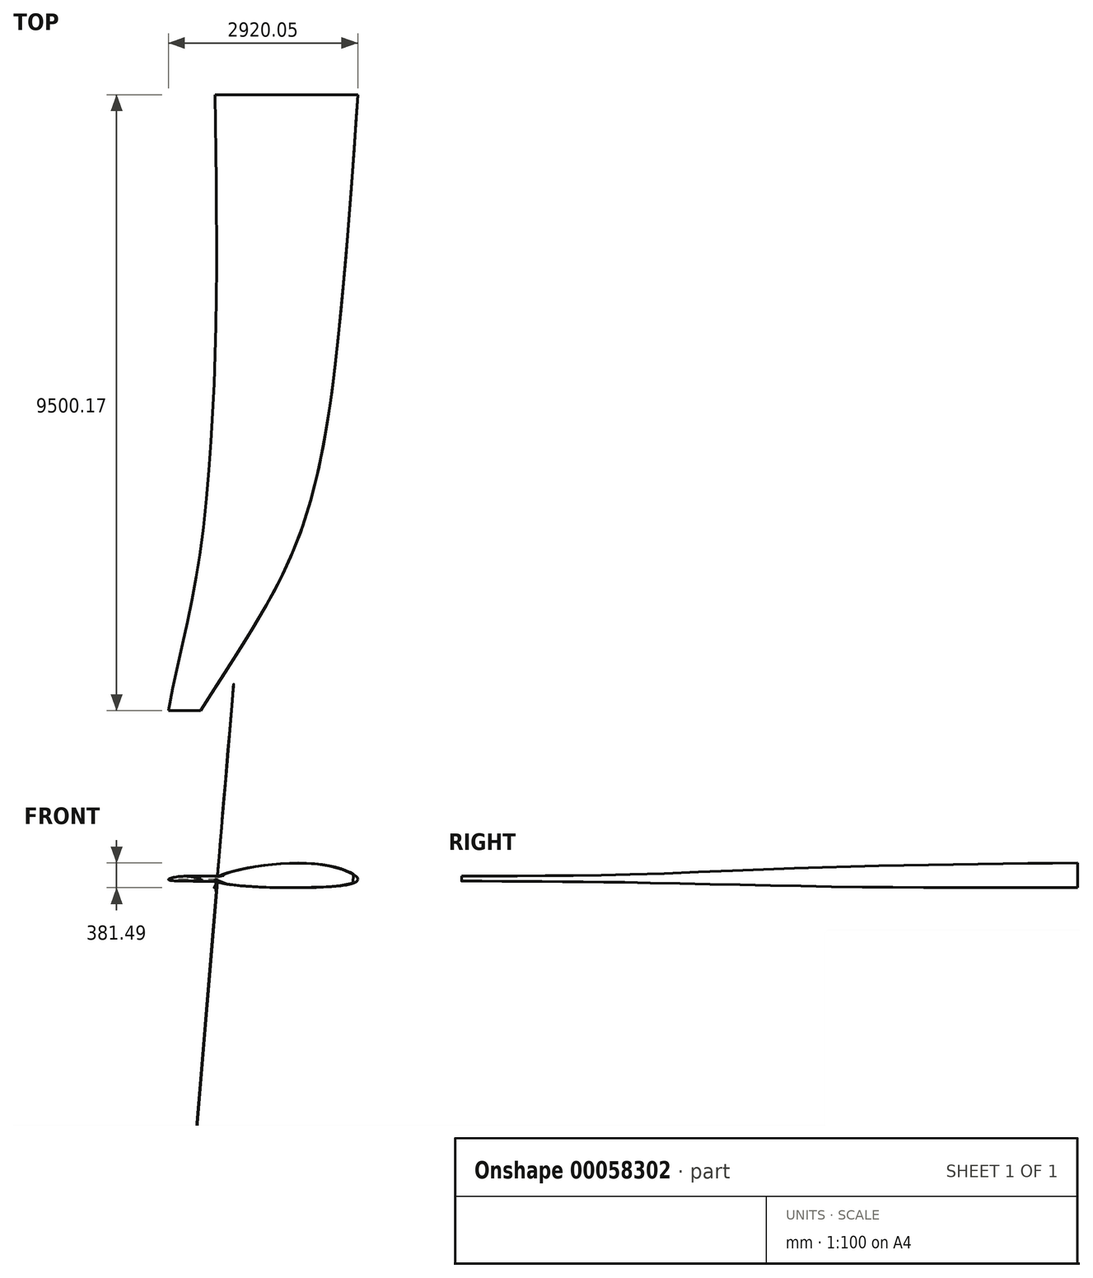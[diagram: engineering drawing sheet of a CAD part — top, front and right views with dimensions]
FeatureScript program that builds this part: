
annotation { "Feature Type Name" : "Feature", "Feature Type Description" : "" }
export const myFeature = defineFeature(function(context is Context, id is Id, definition is map)
    precondition{}
    {
        {
            var Q0;
            Q0=qCreatedBy(makeId("Front.planeOp"),FACE);
            var sketch = newSketch(context, id + "F0", { "sketchPlane" : qUnion([Q0])});
            skLineSegment(sketch, "E0", {"start": v(0, -125) * mm, "end": v(0, 250) * mm, "construction": true});
            skPoint(sketch, "E1", {"position": v(-1440, 0) * mm});
            skPoint(sketch, "E2", {"position": v(760, 0) * mm});
            skFitSpline(sketch, "E3", {"points": [v(-1440, 0) * mm, v(0, 250) * mm, v(760, 0) * mm, v(0, -125) * mm, v(-1440, 0) * mm]});
            skSolve(sketch);
        }
        {
            var Q0;
            Q0=makeQuery(id+"F0.imprint","IMPRINT",FACE,{"disambiguationData":[TD([[makeQuery(id+"F0.imprint","IMPRINT",EDGE,{"derivedFrom":sQuery(id+"F0.wireOp",EDGE,"E3")}),-1.0]])]});
            cPlane(context, id + "F1", {"entities" : qUnion([Q0]), "cplaneType" : CPlaneType.OFFSET, "offset" : 4000 * mm, "width" : 150 * mm, "height" : 150 * mm});
        }
        {
            var Q0;
            Q0=qCreatedBy(id+"F1.planeOp",FACE);
            var Q1;
            Q1 = qBodyType(qCreatedBy(id + "F3" ,EDGE), BodyType.WIRE);
            cPlane(context, id + "F2", {"entities" : qUnion([Q0, Q1]), "cplaneType" : CPlaneType.OFFSET, "offset" : 3000 * mm, "width" : 150 * mm, "height" : 150 * mm});
        }
        {
            var Q0;
            Q0=qCreatedBy(id+"F1.planeOp",FACE);
            var sketch = newSketch(context, id + "F3", { "sketchPlane" : qUnion([Q0])});
            skLineSegment(sketch, "E4", {"start": v(0, 0) * mm, "end": v(-1440, 0) * mm, "construction": true});
            skLineSegment(sketch, "E5", {"start": v(0, 0) * mm, "end": v(430, 0) * mm, "construction": true});
            skLineSegment(sketch, "E6", {"start": v(0, 0) * mm, "end": v(0, 175) * mm, "construction": true});
            skLineSegment(sketch, "E7", {"start": v(0, 0) * mm, "end": v(0, -100) * mm, "construction": true});
            skFitSpline(sketch, "E8", {"points": [v(-1440, 0) * mm, v(0, 175) * mm, v(430, 0) * mm, v(0, -100) * mm, v(-1440, 0) * mm]});
            skSolve(sketch);
        }
        {
            var Q0;
            Q0=qCreatedBy(id+"F2.planeOp",FACE);
            var sketch = newSketch(context, id + "F4", { "sketchPlane" : qUnion([Q0])});
            skLineSegment(sketch, "E9", {"start": v(-1660, 0) * mm, "end": v(-220, 0) * mm, "construction": true});
            skPoint(sketch, "E10", {"position": v(-940, 0) * mm});
            skLineSegment(sketch, "E11", {"start": v(-940, 0) * mm, "end": v(-940, 75) * mm, "construction": true});
            skLineSegment(sketch, "E12", {"start": v(-940, 0) * mm, "end": v(-940, -45) * mm, "construction": true});
            skFitSpline(sketch, "E13", {"points": [v(-1660, 0) * mm, v(-940, 75) * mm, v(-220, 0) * mm, v(-940, -45) * mm, v(-1660, 0) * mm]});
            skSolve(sketch);
        }
        {
            var Q0;
            Q0=qCreatedBy(id+"F2.planeOp",FACE);
            cPlane(context, id + "F5", {"entities" : qUnion([Q0]), "cplaneType" : CPlaneType.OFFSET, "offset" : 2500 * mm, "width" : 150 * mm, "height" : 150 * mm});
        }
        {
            var Q0;
            Q0=qCreatedBy(id+"F5.planeOp",FACE);
            var sketch = newSketch(context, id + "F6", { "sketchPlane" : qUnion([Q0])});
            skLineSegment(sketch, "E14", {"start": v(-2160, 0) * mm, "end": v(-1660, 0) * mm, "construction": true});
            skLineSegment(sketch, "E15", {"start": v(-1910, 0) * mm, "end": v(-1910, 50) * mm, "construction": true});
            skLineSegment(sketch, "E16", {"start": v(-1910, 0) * mm, "end": v(-1910, -25) * mm, "construction": true});
            skFitSpline(sketch, "E17", {"points": [v(-2160, 0) * mm, v(-1910, 50) * mm, v(-1660, 0) * mm, v(-1910, -25) * mm, v(-2160, 0) * mm]});
            skSolve(sketch);
        }
        {
            var Q0;
            Q0=qCreatedBy(makeId("Top.planeOp"),FACE);
            var sketch = newSketch(context, id + "F7", { "sketchPlane" : qUnion([Q0])});
            skPoint(sketch, "E18", {"position": v(760, 0) * mm});
            skPoint(sketch, "E19", {"position": v(430, -4000) * mm});
            skPoint(sketch, "E20", {"position": v(-220, -7000) * mm});
            skPoint(sketch, "E21", {"position": v(-1660, -9500) * mm});
            skFitSpline(sketch, "E22", {"points": [v(760, 0) * mm, v(430, -4000) * mm, v(-220, -7000) * mm, v(-1660, -9500) * mm], "startDerivative": vector(-744.8, -11209.75) * mm, "endDerivative": vector(-4861.61, -7845.53) * mm});
            skSolve(sketch);
        }
        {
            var Q0;
            Q0=makeQuery(id+"F0.imprint","IMPRINT",FACE,{"disambiguationData":[TD([[makeQuery(id+"F0.imprint","IMPRINT",EDGE,{"derivedFrom":sQuery(id+"F0.wireOp",EDGE,"E3")}),-1.0]])]});
            var Q1;
            Q1=makeQuery(id+"F3.imprint","IMPRINT",FACE,{"disambiguationData":[TD([[makeQuery(id+"F3.imprint","IMPRINT",EDGE,{"derivedFrom":sQuery(id+"F3.wireOp",EDGE,"E8")}),-1.0]])]});
            var Q2;
            Q2=makeQuery(id+"F4.imprint","IMPRINT",FACE,{"disambiguationData":[TD([[makeQuery(id+"F4.imprint","IMPRINT",EDGE,{"derivedFrom":sQuery(id+"F4.wireOp",EDGE,"E13")}),-1.0]])]});
            var Q3;
            Q3=makeQuery(id+"F6.imprint","IMPRINT",FACE,{"disambiguationData":[TD([[makeQuery(id+"F6.imprint","IMPRINT",EDGE,{"derivedFrom":sQuery(id+"F6.wireOp",EDGE,"E17")}),-1.0]])]});
            var Q4;
            Q4=sQuery(id+"F7.wireOp",EDGE,"E22");
            loft(context, id + "F8", {"addGuides" : true, "sheetProfilesArray" : [{ "sheetProfileEntities" : qUnion([Q0]) }, { "sheetProfileEntities" : qUnion([Q1]) }, { "sheetProfileEntities" : qUnion([Q2]) }, { "sheetProfileEntities" : qUnion([Q3]) }], "guidesArray" : [{ "guideEntities" : qUnion([Q4]), "guideDerivativeType" : LoftGuideDerivativeType.DEFAULT, "guideDerivativeMagnitude" : 1 }]});
        }
        {
            var Q0;
            Q0=makeQuery(id+"F8.opLoft","CAP_FACE",FACE,{"disambiguationData":[OSD([makeQuery(id+"F0.imprint","IMPRINT",FACE,{"disambiguationData":[TD([[makeQuery(id+"F0.imprint","IMPRINT",EDGE,{"derivedFrom":sQuery(id+"F0.wireOp",EDGE,"E3")}),-1.0]])]})])],"isStart":true});
            shell(context, id + "F9", {"entities" : qUnion([Q0]), "thickness" : 2.5 * mm});
        }
    });
